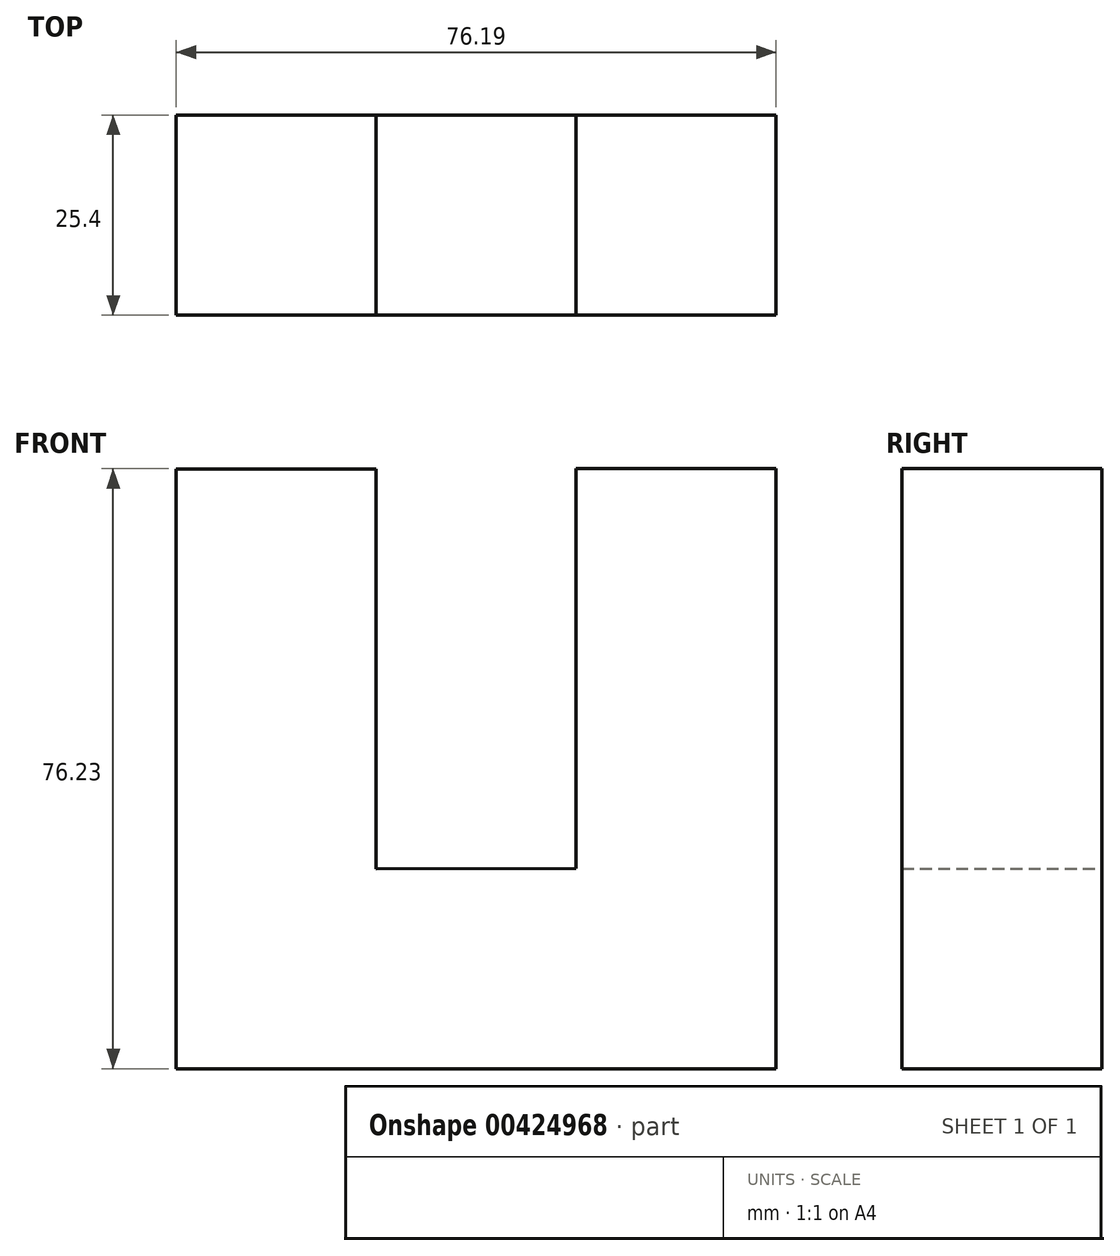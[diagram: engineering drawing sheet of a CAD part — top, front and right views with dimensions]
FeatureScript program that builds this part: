
annotation { "Feature Type Name" : "Feature", "Feature Type Description" : "" }
export const myFeature = defineFeature(function(context is Context, id is Id, definition is map)
    precondition{}
    {
        {
            var Q0;
            Q0=qCreatedBy(makeId("Front.planeOp"),FACE);
            var sketch = newSketch(context, id + "F0", { "sketchPlane" : qUnion([Q0])});
            skLineSegment(sketch, "E0", {"start": v(0, 0) * mm, "end": v(-76.2, 0) * mm});
            skLineSegment(sketch, "E1", {"start": v(-76.2, 0) * mm, "end": v(-76.2, 76.2) * mm});
            skLineSegment(sketch, "E2", {"start": v(-76.2, 76.2) * mm, "end": v(-50.8, 76.2) * mm});
            skLineSegment(sketch, "E3", {"start": v(-50.8, 76.2) * mm, "end": v(-50.8, 25.4) * mm});
            skLineSegment(sketch, "E4", {"start": v(0, 0) * mm, "end": v(0, 76.23) * mm});
            skLineSegment(sketch, "E5", {"start": v(0, 76.23) * mm, "end": v(-25.4, 76.23) * mm});
            skLineSegment(sketch, "E6", {"start": v(-25.4, 76.23) * mm, "end": v(-25.4, 25.43) * mm});
            skLineSegment(sketch, "E7", {"start": v(-25.4, 25.43) * mm, "end": v(-50.8, 25.4) * mm});
            skSolve(sketch);
        }
        {
            var Q0;
            Q0 = qSketchRegion(id + "F0", true);
            extrude(context, id + "F1", {"entities" : qUnion([Q0]), "depth" : 25.4 * mm});
        }
    });
